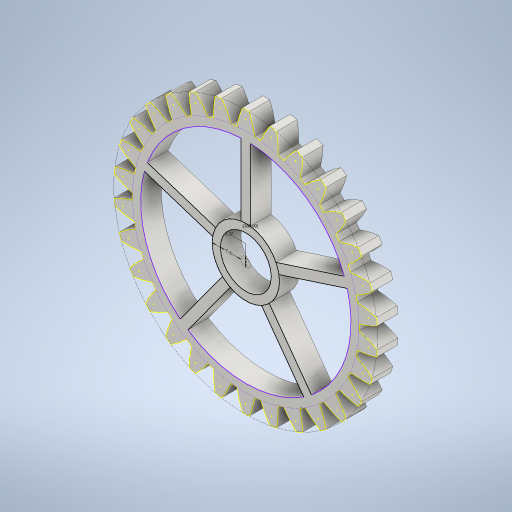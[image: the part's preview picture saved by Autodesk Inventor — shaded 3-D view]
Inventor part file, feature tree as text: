
AUTODESK INVENTOR PART (.ipt)
format: ipt  version: 2023 (Build 270158000, 158)  size: 572,928 bytes
history: native  units: mm (DEFAULTED — no unit token found)
features: plane x3, other x3, sketch x3, extrude x2, projected_geometry x1
ambient origin geometry x8: Origin, YZ Plane, XZ Plane, XY Plane, X Axis, Y Axis, Z Axis, Center Point
bodies: Solid1 (feature_tree)
feature tree (12):
  extrude  "Extrusion1"  Depth=5.0mm TaperAngle=0.0deg
  plane  "Work Plane2"
  plane  "Work Plane8"
  plane  "Work Plane9"
  other  "Spur Gear"
  extrude  "Extrusion2"  Depth=10.0mm TaperAngle=0.0deg
  sketch  "Sketch1"  dims[d0=64.0mm d1=5.0mm d2=0.0mm]
  sketch  "Sketch2"  dims[d3=60.0mm d4=10.0mm d5=0.0mm]
  other  "Srf1"
  sketch  "Sketch3"  dims[d16=40.0mm d17=0.0mm d34=1.047198mm d39=0.0mm d41=0.0mm d43=40.0mm d46=40.0mm d47=0.0mm d48=0.0mm d49=2.32mm d50=7.0mm d51=2.0mm d52=50.0mm d54=360.0deg d56=0.0mm d57=0.0mm d58=5.0mm d59=0.5mm d60=0.872665mm d61=0.5mm d62=0.872665mm]
  projected_geometry  "Projected Loop1"
  other  "Pitch Diameter"
